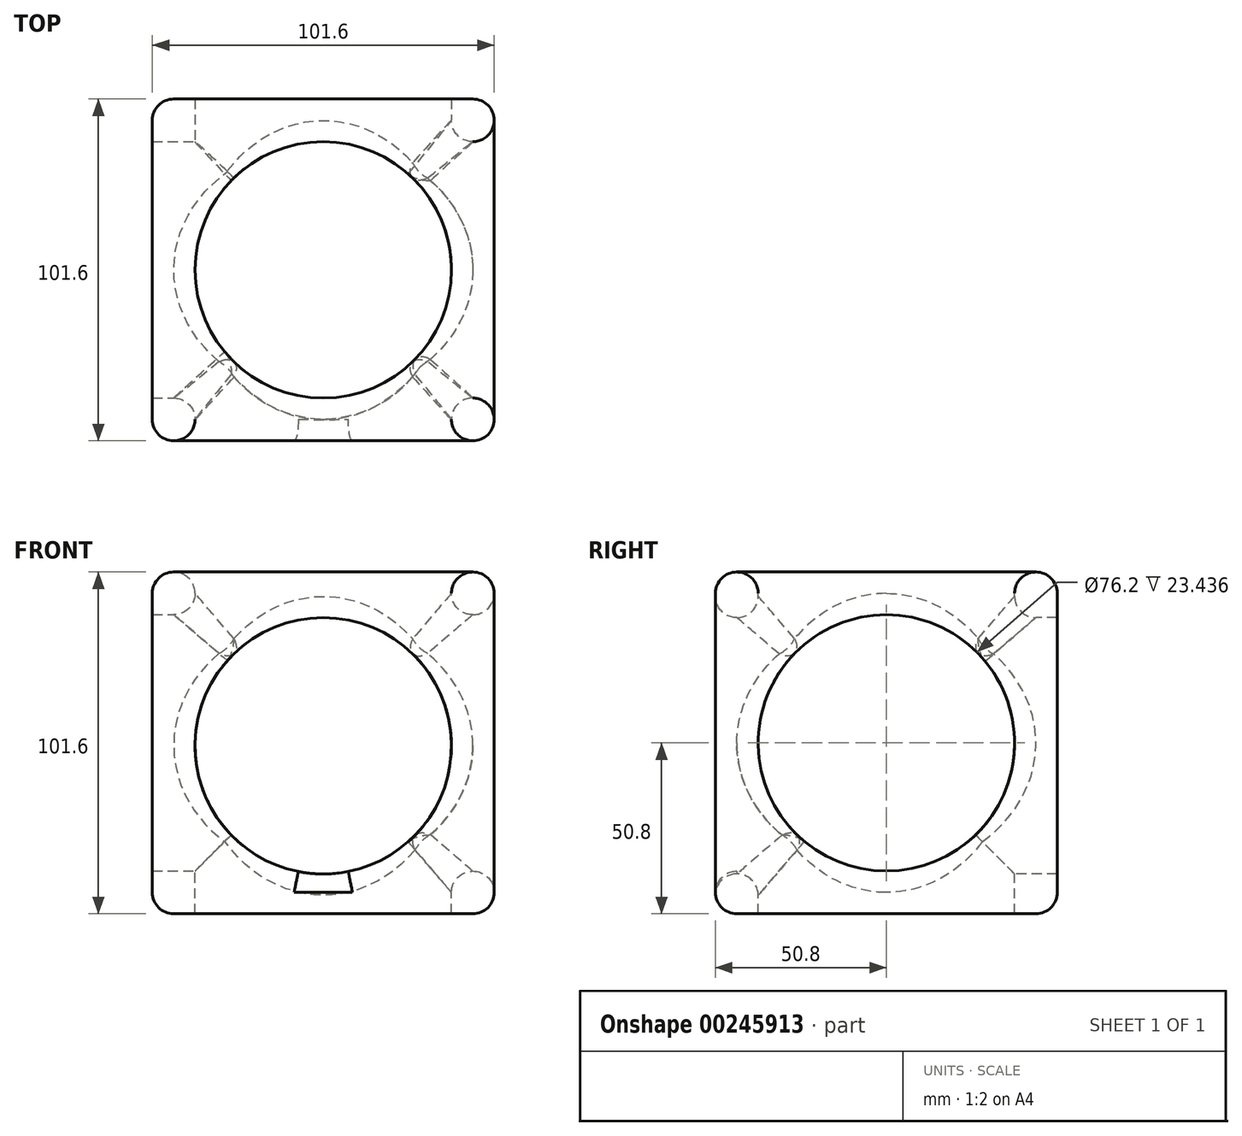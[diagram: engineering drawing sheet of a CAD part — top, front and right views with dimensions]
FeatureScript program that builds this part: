
annotation { "Feature Type Name" : "Feature", "Feature Type Description" : "" }
export const myFeature = defineFeature(function(context is Context, id is Id, definition is map)
    precondition{}
    {
        {
            var Q0;
            Q0=qCreatedBy(makeId("Front.planeOp"),FACE);
            var sketch = newSketch(context, id + "F0", { "sketchPlane" : qUnion([Q0])});
            skLineSegment(sketch, "E0", {"start": v(0, 0) * mm, "end": v(101.6, 0) * mm});
            skLineSegment(sketch, "E1", {"start": v(101.6, 0) * mm, "end": v(101.6, 101.6) * mm});
            skLineSegment(sketch, "E2", {"start": v(101.6, 101.6) * mm, "end": v(0, 101.6) * mm});
            skLineSegment(sketch, "E3", {"start": v(0, 101.6) * mm, "end": v(0, 0) * mm});
            skSolve(sketch);
        }
        {
            var Q0;
            Q0=makeQuery(id+"F0.imprint","IMPRINT",FACE,{"disambiguationData":[TD([[makeQuery(id+"F0.imprint","IMPRINT",EDGE,{"derivedFrom":sQuery(id+"F0.wireOp",EDGE,"E0")}),1.0]])]});
            extrude(context, id + "F1", {"entities" : qUnion([Q0]), "depth" : 101.6 * mm});
        }
        {
            var Q0;
            Q0=makeQuery(id+"F1.opExtrude","CAP_FACE",FACE,{"disambiguationData":[OSD([sQuery(id+"F0.wireOp",EDGE,"E0"),sQuery(id+"F0.wireOp",EDGE,"E1"),sQuery(id+"F0.wireOp",EDGE,"E2"),sQuery(id+"F0.wireOp",EDGE,"E3")])],"isStart":false});
            var sketch = newSketch(context, id + "F2", { "sketchPlane" : qUnion([Q0])});
            skPoint(sketch, "E4.orphan", {"position": v(50.8, 101.6) * mm});
            skLineSegment(sketch, "E5", {"start": v(50.8, 104.22) * mm, "end": v(50.8, 101.6) * mm});
            skCircle(sketch, "E6", {"center": v(50.8, 49.95) * mm, "radius": 38.1 * mm});
            skPoint(sketch, "E7.trimOffspring.end.orphan", {"position": v(50.8, -4.33) * mm});
            skSolve(sketch);
        }
        {
            var Q0;
            Q0=makeQuery(id+"F2.imprint","IMPRINT",FACE,{"disambiguationData":[TD([[makeQuery(id+"F2.imprint","IMPRINT",EDGE,{"derivedFrom":sQuery(id+"F2.wireOp",EDGE,"E6")}),1.0]])]});
            extrude(context, id + "F3", {"entities" : qUnion([Q0]), "operationType" : NewBodyOperationType.REMOVE, "oppositeDirection" : true, "depth" : 101.6 * mm});
        }
        {
            var Q0;
            Q0=makeQuery(id+"F1.opExtrude","SWEPT_FACE",FACE,{"disambiguationData":[OSD([sQuery(id+"F0.wireOp",EDGE,"E2")])]});
            var sketch = newSketch(context, id + "F4", { "sketchPlane" : qUnion([Q0])});
            skCircle(sketch, "E8", {"center": v(50.8, -50.8) * mm, "radius": 38.1 * mm});
            skPoint(sketch, "E9.orphan", {"position": v(50.8, 0) * mm});
            skPoint(sketch, "E10.end.orphan", {"position": v(50.8, -101.6) * mm});
            skSolve(sketch);
        }
        {
            var Q0;
            Q0 = qSketchRegion(id + "F4", true);
            extrude(context, id + "F5", {"entities" : qUnion([Q0]), "operationType" : NewBodyOperationType.REMOVE, "oppositeDirection" : true, "depth" : 101.6 * mm});
        }
        {
            var Q0;
            Q0=makeQuery(id+"F1.opExtrude","SWEPT_FACE",FACE,{"disambiguationData":[OSD([sQuery(id+"F0.wireOp",EDGE,"E1")])]});
            var sketch = newSketch(context, id + "F6", { "sketchPlane" : qUnion([Q0])});
            skPoint(sketch, "E11.start.orphan", {"position": v(-50.8, 101.6) * mm});
            skLineSegment(sketch, "E12", {"start": v(-50.8, 101.6) * mm, "end": v(-50.8, 0) * mm});
            skCircle(sketch, "E13", {"center": v(-50.8, 50.8) * mm, "radius": 38.1 * mm});
            skSolve(sketch);
        }
        {
            var Q0;
            Q0 = qSketchRegion(id + "F6", true);
            extrude(context, id + "F7", {"entities" : qUnion([Q0]), "operationType" : NewBodyOperationType.REMOVE, "oppositeDirection" : true, "depth" : 101.6 * mm});
        }
        {
            var Q0;
            Q0=makeQuery(id+"F1.opExtrude","SWEPT_EDGE",EDGE,{"disambiguationData":[OSD([sQuery(id+"F0.wireOp",EDGE,"E2"),sQuery(id+"F0.wireOp",EDGE,"E3")])]});
            var Q1;
            Q1=makeQuery(id+"F1.opExtrude","CAP_EDGE",EDGE,{"disambiguationData":[OSD([sQuery(id+"F0.wireOp",EDGE,"E2")])],"isStart":false});
            var Q2;
            Q2=makeQuery(id+"F1.opExtrude","SWEPT_EDGE",EDGE,{"disambiguationData":[OSD([sQuery(id+"F0.wireOp",EDGE,"E1"),sQuery(id+"F0.wireOp",EDGE,"E2")])]});
            var Q3;
            Q3=makeQuery(id+"F1.opExtrude","CAP_EDGE",EDGE,{"disambiguationData":[OSD([sQuery(id+"F0.wireOp",EDGE,"E2")])],"isStart":true});
            var Q4;
            Q4=makeQuery(id+"F1.opExtrude","SWEPT_EDGE",EDGE,{"disambiguationData":[OSD([sQuery(id+"F0.wireOp",EDGE,"E0"),sQuery(id+"F0.wireOp",EDGE,"E1")])]});
            var Q5;
            Q5=makeQuery(id+"F1.opExtrude","CAP_EDGE",EDGE,{"disambiguationData":[OSD([sQuery(id+"F0.wireOp",EDGE,"E1")])],"isStart":false});
            var Q6;
            Q6=makeQuery(id+"F1.opExtrude","CAP_EDGE",EDGE,{"disambiguationData":[OSD([sQuery(id+"F0.wireOp",EDGE,"E1")])],"isStart":true});
            var Q7;
            Q7=makeQuery(id+"F1.opExtrude","CAP_EDGE",EDGE,{"disambiguationData":[OSD([sQuery(id+"F0.wireOp",EDGE,"E0")])],"isStart":false});
            var Q8;
            Q8=makeQuery(id+"F1.opExtrude","CAP_EDGE",EDGE,{"disambiguationData":[OSD([sQuery(id+"F0.wireOp",EDGE,"E3")])],"isStart":false});
            var Q9;
            Q9=makeQuery(id+"F1.opExtrude","SWEPT_EDGE",EDGE,{"disambiguationData":[OSD([sQuery(id+"F0.wireOp",EDGE,"E0"),sQuery(id+"F0.wireOp",EDGE,"E3")])]});
            var Q10;
            Q10=makeQuery(id+"F1.opExtrude","CAP_EDGE",EDGE,{"disambiguationData":[OSD([sQuery(id+"F0.wireOp",EDGE,"E0")])],"isStart":true});
            var Q11;
            Q11=makeQuery(id+"F1.opExtrude","CAP_EDGE",EDGE,{"disambiguationData":[OSD([sQuery(id+"F0.wireOp",EDGE,"E3")])],"isStart":true});
            fillet(context, id + "F8", {"entities" : qUnion([Q0, Q1, Q2, Q3, Q4, Q5, Q6, Q7, Q8, Q9, Q10, Q11]), "radius" : 6.35 * mm, "tangentPropagation" : true, "allowEdgeOverflow" : false});
        }
        {
            var Q0;
            {var subQ0=makeQuery(id+"F5.opExtrude","SWEPT_FACE",FACE,{"disambiguationData":[OSD([sQuery(id+"F4.wireOp",EDGE,"E8")])]});Q0=makeQuery(id+"F5.boolean.opBoolean","COPY",FACE,{"disambiguationData":[TD([makeQuery(id+"F1.opExtrude","SWEPT_FACE",FACE,{"disambiguationData":[OSD([sQuery(id+"F0.wireOp",EDGE,"E2")])]})])],"derivedFrom":subQ0});}
            var Q1;
            Q1=makeQuery(id+"F7.boolean.opBoolean","COPY",FACE,{"disambiguationData":[TD([makeQuery(id+"F1.opExtrude","SWEPT_FACE",FACE,{"disambiguationData":[OSD([sQuery(id+"F0.wireOp",EDGE,"E1")])]})])],"derivedFrom":makeQuery(id+"F7.opExtrude","SWEPT_FACE",FACE,{"disambiguationData":[OSD([sQuery(id+"F6.wireOp",EDGE,"E13")])]})});
            var Q2;
            {var subQ0=makeQuery(id+"F3.boolean.opBoolean","COPY",FACE,{"derivedFrom":makeQuery(id+"F3.opExtrude","SWEPT_FACE",FACE,{"disambiguationData":[OSD([sQuery(id+"F2.wireOp",EDGE,"E6")])]})});Q2=makeQuery(id+"F5.boolean.opBoolean","SPLIT",FACE,{"disambiguationData":[TD([makeQuery(id+"F1.opExtrude","CAP_FACE",FACE,{"disambiguationData":[OSD([sQuery(id+"F0.wireOp",EDGE,"E0"),sQuery(id+"F0.wireOp",EDGE,"E1"),sQuery(id+"F0.wireOp",EDGE,"E2"),sQuery(id+"F0.wireOp",EDGE,"E3")])],"isStart":false})])],"derivedFrom":subQ0});}
            var Q3;
            Q3=makeQuery(id+"F7.boolean.opBoolean","COPY",EDGE,{"derivedFrom":makeQuery(id+"F7.opExtrude","CAP_EDGE",EDGE,{"disambiguationData":[OSD([sQuery(id+"F6.wireOp",EDGE,"E13")])],"isStart":false})});
            var Q4;
            Q4=makeQuery(id+"F3.boolean.opBoolean","COPY",EDGE,{"derivedFrom":makeQuery(id+"F3.opExtrude","CAP_EDGE",EDGE,{"disambiguationData":[OSD([sQuery(id+"F2.wireOp",EDGE,"E6")])],"isStart":false})});
            var Q5;
            Q5=makeQuery(id+"F5.boolean.opBoolean","COPY",EDGE,{"derivedFrom":makeQuery(id+"F5.opExtrude","CAP_EDGE",EDGE,{"disambiguationData":[OSD([sQuery(id+"F4.wireOp",EDGE,"E8")])],"isStart":false})});
            fillet(context, id + "F9", {"entities" : qUnion([Q0, Q1, Q2, Q3, Q4, Q5]), "radius" : 6.35 * mm, "tangentPropagation" : true, "allowEdgeOverflow" : false});
        }
    });
